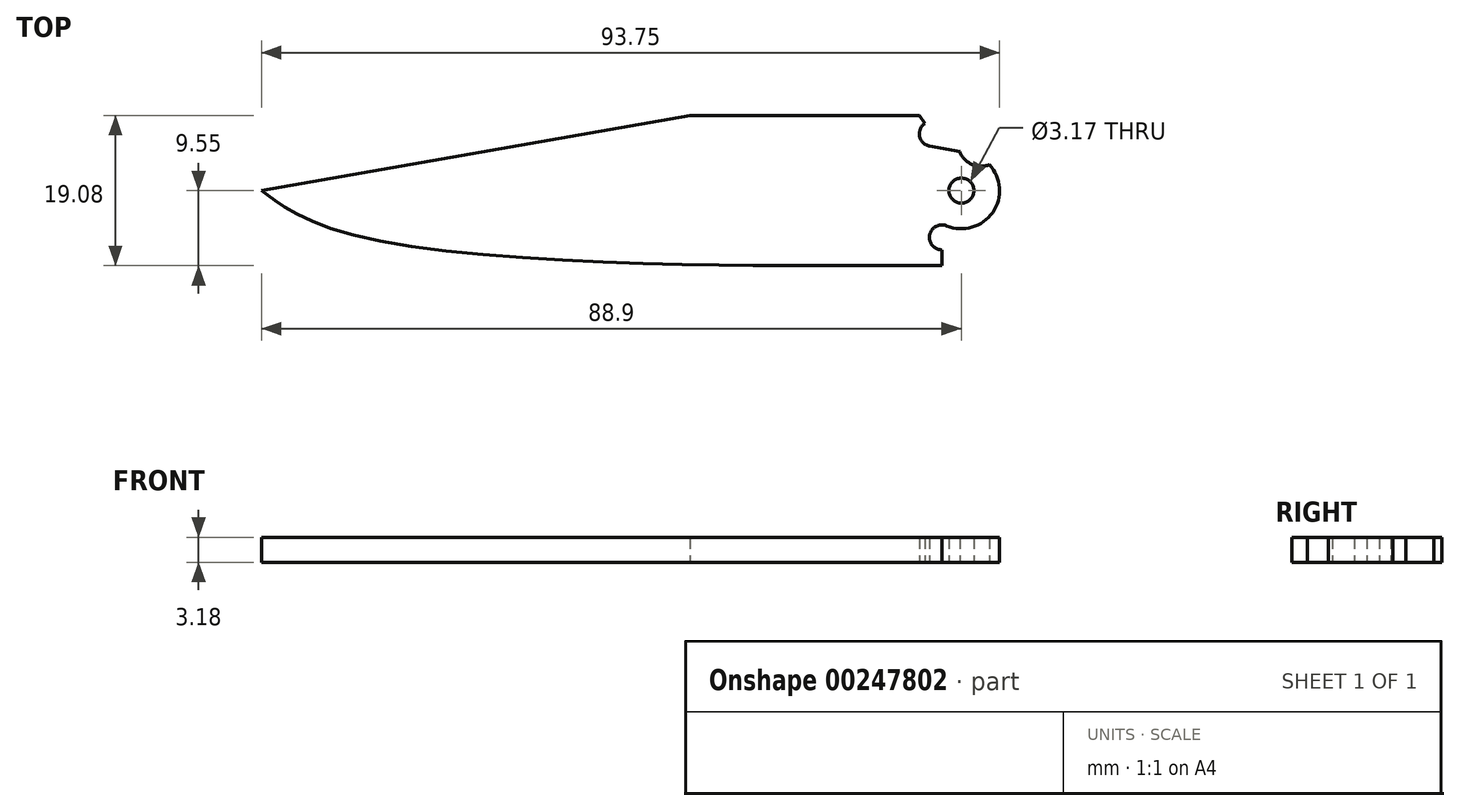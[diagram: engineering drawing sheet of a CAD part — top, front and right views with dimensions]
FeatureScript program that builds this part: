
annotation { "Feature Type Name" : "Feature", "Feature Type Description" : "" }
export const myFeature = defineFeature(function(context is Context, id is Id, definition is map)
    precondition{}
    {
        {
            var Q0;
            Q0=qCreatedBy(makeId("Top.planeOp"),FACE);
            var sketch = newSketch(context, id + "F0", { "sketchPlane" : qUnion([Q0])});
            skCircle(sketch, "E0", {"center": v(0, 0) * mm, "radius": 3.33 * mm, "construction": true});
            skCircle(sketch, "E1", {"center": v(0, 0) * mm, "radius": 1.85 * mm, "construction": true});
            skCircle(sketch, "E2", {"center": v(-3.75, 7.21) * mm, "radius": 1.59 * mm, "construction": true});
            skCircle(sketch, "E3", {"center": v(2.48, 5.94) * mm, "radius": 2.86 * mm, "construction": true});
            skCircle(sketch, "E4", {"center": v(2.48, 5.94) * mm, "radius": 1.27 * mm, "construction": true});
            skCircle(sketch, "E5", {"center": v(-2.48, -5.94) * mm, "radius": 2.86 * mm, "construction": true});
            skCircle(sketch, "E6", {"center": v(-2.48, -5.94) * mm, "radius": 1.27 * mm, "construction": true});
            skLineSegment(sketch, "E7", {"start": v(-2.48, -5.94) * mm, "end": v(2.48, 5.94) * mm, "construction": true});
            skCircle(sketch, "E8", {"center": v(0, 0) * mm, "radius": 4.85 * mm, "construction": true});
            skLineSegment(sketch, "E9", {"start": v(-5.33, 7.21) * mm, "end": v(-5.33, -5.94) * mm, "construction": true});
            skLineSegment(sketch, "E10", {"start": v(-3.75, 8.8) * mm, "end": v(2.48, 8.8) * mm, "construction": true});
            skLineSegment(sketch, "E11", {"start": v(-7.87, 11.34) * mm, "end": v(14.85, 11.34) * mm, "construction": true});
            skLineSegment(sketch, "E12", {"start": v(-7.87, -11.34) * mm, "end": v(15.72, -11.34) * mm, "construction": true});
            skLineSegment(sketch, "E13", {"start": v(-7.87, 11.34) * mm, "end": v(-7.87, -11.34) * mm, "construction": true});
            skLineSegment(sketch, "E14", {"start": v(-7.87, 0) * mm, "end": v(0, 0) * mm, "construction": true});
            skSolve(sketch);
        }
        {
            var Q0;
            Q0=qCreatedBy(makeId("Top.planeOp"),FACE);
            var sketch = newSketch(context, id + "F1", { "sketchPlane" : qUnion([Q0])});
            skCircle(sketch, "E15", {"center": v(0, 0) * mm, "radius": 1.59 * mm});
            skArc(sketch, "E16", {"start": v(-4.64, 8.52) * mm, "mid": v(-5.3, 6.88) * mm, "end": v(-4.03, 5.65) * mm});
            skArc(sketch, "E17", {"start": v(-0.2, 4.97) * mm, "mid": v(1.32, 3.33) * mm, "end": v(3.56, 3.3) * mm});
            skLineSegment(sketch, "E18", {"start": v(-5.33, 9.53) * mm, "end": v(-34.5, 9.53) * mm});
            skLineSegment(sketch, "E19", {"start": v(-4.03, 5.65) * mm, "end": v(-0.2, 4.97) * mm});
            skLineSegment(sketch, "E20", {"start": v(-34.5, 9.53) * mm, "end": v(-88.9, 0) * mm});
            skFitSpline(sketch, "E21", {"points": [v(-88.9, 0) * mm, v(-75.38, -6.1) * mm, v(-13.67, -9.53) * mm], "startDerivative": vector(15.16, -10.73) * mm, "endDerivative": vector(13.6, 0) * mm});
            skArc(sketch, "E22.trimOffspring", {"start": v(-1.87, -4.48) * mm, "mid": v(3.98, -2.77) * mm, "end": v(3.56, 3.3) * mm});
            skLineSegment(sketch, "E23", {"start": v(-5.33, 9.53) * mm, "end": v(-4.64, 8.52) * mm});
            skLineSegment(sketch, "E24", {"start": v(-2.48, -7.53) * mm, "end": v(-2.48, -9.53) * mm});
            skLineSegment(sketch, "E25", {"start": v(-2.48, -9.53) * mm, "end": v(-13.67, -9.53) * mm});
            skArc(sketch, "E26", {"start": v(-1.87, -4.48) * mm, "mid": v(-4.03, -5.63) * mm, "end": v(-2.48, -7.53) * mm});
            skSolve(sketch);
        }
        {
            var Q0;
            Q0=makeQuery(id+"F1.imprint","IMPRINT",FACE,{"disambiguationData":[TD([[makeQuery(id+"F1.imprint","IMPRINT",EDGE,{"derivedFrom":sQuery(id+"F1.wireOp",EDGE,"E15")}),-1.0]])]});
            extrude(context, id + "F2", {"entities" : qUnion([Q0]), "depth" : 3.17 * mm});
        }
    });
